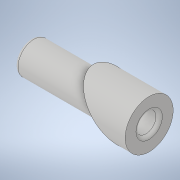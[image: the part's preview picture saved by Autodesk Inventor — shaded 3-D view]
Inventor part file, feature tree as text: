
AUTODESK INVENTOR PART (.ipt)
format: ipt  version: 2020 (Build 240168000, 168)  size: 135,680 bytes
history: native  units: in
note: dims shown in document units (in); Inventor stores cm internally (conversion verified against a paired STEP export)
features: sketch x3, extrude x3, plane x2, fillet x1
ambient origin geometry x8: Origin, YZ Plane, XZ Plane, XY Plane, X Axis, Y Axis, Z Axis, Center Point
bodies: Body1 (feature_tree)
feature tree (9):
  plane  "Work Plane1"
  sketch  "Sketch1"  dims[d0=45.0deg d6=1.0in d7=0.0in]
  plane  "Work Plane2"
  extrude  "Extrusion2"  Depth=1.0in TaperAngle=0.0deg
  extrude  "Extrusion4"  Depth=3.0in TaperAngle=0.0deg
  extrude  "Extrusion5"  [1 undecoded]
  fillet  "Fillet1"  [1 undecoded]
  sketch  "Sketch3"  dims[d13=0.0in d15=3.0in d16=0.0in]
  sketch  "Sketch4"  dims[d17=0.1in]
note: 2 required parameter values undecoded (feature->parameter linkage not recoverable at this tier; creation-order binding heuristic only, values carry confidence <= 0.55)
